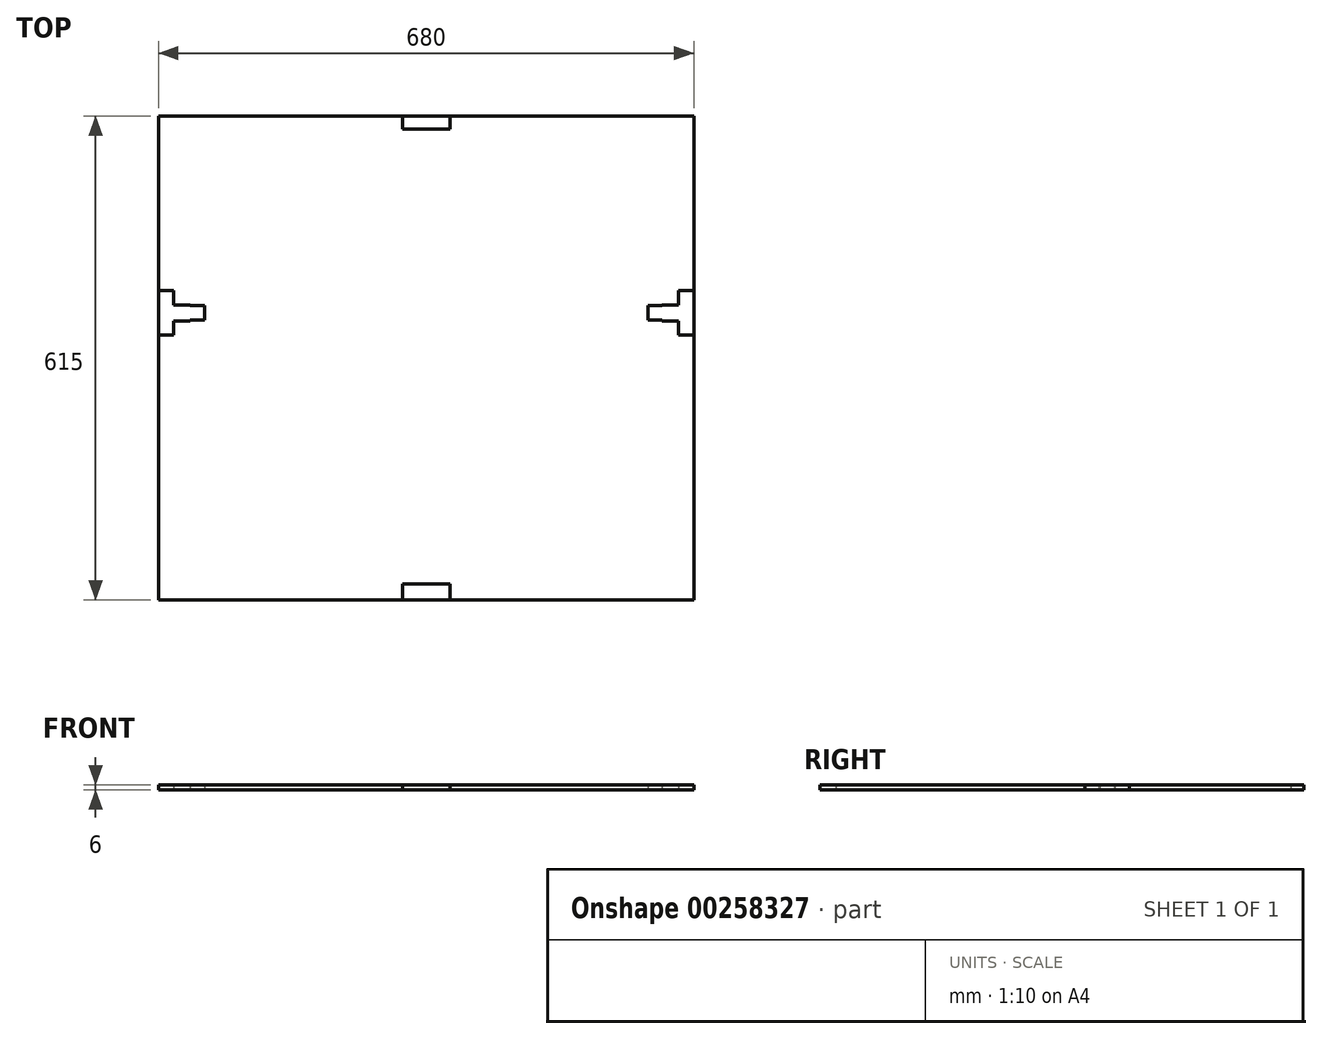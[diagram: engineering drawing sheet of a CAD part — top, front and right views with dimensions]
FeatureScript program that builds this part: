
annotation { "Feature Type Name" : "Feature", "Feature Type Description" : "" }
export const myFeature = defineFeature(function(context is Context, id is Id, definition is map)
    precondition{}
    {
        {
            var Q0;
            Q0=qCreatedBy(makeId("Top.planeOp"),FACE);
            var sketch = newSketch(context, id + "F0", { "sketchPlane" : qUnion([Q0])});
            skLineSegment(sketch, "E0.bottom", {"start": v(340, -307.5) * mm, "end": v(30.2, -307.5) * mm});
            skLineSegment(sketch, "E0.top", {"start": v(340, 307.5) * mm, "end": v(30.2, 307.5) * mm});
            skLineSegment(sketch, "E0.left", {"start": v(340, -307.5) * mm, "end": v(340, 29.3) * mm});
            skLineSegment(sketch, "E0.right", {"start": v(-340, -307.5) * mm, "end": v(-340, 29.3) * mm});
            skPoint(sketch, "E0.middle", {"position": v(0, 0) * mm});
            skLineSegment(sketch, "E1", {"start": v(0, 307.5) * mm, "end": v(0, -307.5) * mm, "construction": true});
            skLineSegment(sketch, "E2", {"start": v(-30.2, 307.5) * mm, "end": v(-30.2, 291.1) * mm});
            skLineSegment(sketch, "E3", {"start": v(-30.2, 291.1) * mm, "end": v(30.2, 291.1) * mm});
            skLineSegment(sketch, "E4", {"start": v(30.2, 291.1) * mm, "end": v(30.2, 307.5) * mm});
            skLineSegment(sketch, "E5.trimOffspring", {"start": v(-30.2, 307.5) * mm, "end": v(-340, 307.5) * mm});
            skLineSegment(sketch, "E6.trimOffspring", {"start": v(-30.2, -307.5) * mm, "end": v(-340, -307.5) * mm});
            skLineSegment(sketch, "E7", {"start": v(-30.2, -307.5) * mm, "end": v(-30.2, -287.1) * mm});
            skLineSegment(sketch, "E8", {"start": v(-30.2, -287.1) * mm, "end": v(30.2, -287.1) * mm});
            skLineSegment(sketch, "E9", {"start": v(30.2, -287.1) * mm, "end": v(30.2, -307.5) * mm});
            skLineSegment(sketch, "E10", {"start": v(-340, 85.7) * mm, "end": v(-320.8, 85.7) * mm});
            skLineSegment(sketch, "E11", {"start": v(-320.8, 85.7) * mm, "end": v(-320.8, 67.7) * mm});
            skLineSegment(sketch, "E12", {"start": v(-299.6, 48.3) * mm, "end": v(-281.6, 48.3) * mm});
            skLineSegment(sketch, "E13", {"start": v(-281.6, 66.7) * mm, "end": v(-281.6, 48.3) * mm});
            skLineSegment(sketch, "E14", {"start": v(-281.6, 66.7) * mm, "end": v(-299.6, 66.7) * mm});
            skLineSegment(sketch, "E15", {"start": v(-320.8, 29.3) * mm, "end": v(-340, 29.3) * mm});
            skLineSegment(sketch, "E16", {"start": v(-299.6, 66.7) * mm, "end": v(-299.6, 67.7) * mm});
            skLineSegment(sketch, "E17", {"start": v(-299.6, 67.7) * mm, "end": v(-320.8, 67.7) * mm});
            skLineSegment(sketch, "E18", {"start": v(-299.6, 48.3) * mm, "end": v(-299.6, 47.3) * mm});
            skLineSegment(sketch, "E19", {"start": v(-299.6, 47.3) * mm, "end": v(-320.8, 47.3) * mm});
            skLineSegment(sketch, "E20.trimOffspring", {"start": v(-320.8, 47.3) * mm, "end": v(-320.8, 29.3) * mm});
            skLineSegment(sketch, "E21.trimOffspring", {"start": v(-340, 85.7) * mm, "end": v(-340, 307.5) * mm});
            skLineSegment(sketch, "E22.MirrorCS", {"start": v(299.6, 48.3) * mm, "end": v(299.6, 47.3) * mm});
            skLineSegment(sketch, "E23.MirrorCS", {"start": v(299.6, 66.7) * mm, "end": v(299.6, 67.7) * mm});
            skLineSegment(sketch, "E24.MirrorCS", {"start": v(299.6, 47.3) * mm, "end": v(320.8, 47.3) * mm});
            skLineSegment(sketch, "E25.MirrorCS", {"start": v(320.8, 29.3) * mm, "end": v(340, 29.3) * mm});
            skLineSegment(sketch, "E26.MirrorCS", {"start": v(299.6, 67.7) * mm, "end": v(320.8, 67.7) * mm});
            skLineSegment(sketch, "E27.MirrorCS", {"start": v(281.6, 66.7) * mm, "end": v(281.6, 48.3) * mm});
            skLineSegment(sketch, "E28.MirrorCS", {"start": v(320.8, 47.3) * mm, "end": v(320.8, 29.3) * mm});
            skLineSegment(sketch, "E29.MirrorCS", {"start": v(340, 85.7) * mm, "end": v(320.8, 85.7) * mm});
            skLineSegment(sketch, "E30.MirrorCS", {"start": v(299.6, 48.3) * mm, "end": v(281.6, 48.3) * mm});
            skLineSegment(sketch, "E31.MirrorCS", {"start": v(281.6, 66.7) * mm, "end": v(299.6, 66.7) * mm});
            skLineSegment(sketch, "E32.MirrorCS", {"start": v(320.8, 85.7) * mm, "end": v(320.8, 67.7) * mm});
            skLineSegment(sketch, "E33.trimOffspring", {"start": v(340, 85.7) * mm, "end": v(340, 307.5) * mm});
            skLineSegment(sketch, "E34", {"start": v(-330, 85.7) * mm, "end": v(-330, 29.3) * mm, "construction": true});
            skLineSegment(sketch, "E35", {"start": v(-281.6, 57.5) * mm, "end": v(-330, 57.5) * mm, "construction": true});
            skSolve(sketch);
        }
        {
            var Q0;
            Q0=qCreatedBy(makeId("Top.planeOp"),FACE);
            var sketch = newSketch(context, id + "F1", { "sketchPlane" : qUnion([Q0])});
            skLineSegment(sketch, "E36.bottom", {"start": v(-340, 307.5) * mm, "end": v(340, 307.5) * mm});
            skLineSegment(sketch, "E36.top", {"start": v(-340, -307.5) * mm, "end": v(340, -307.5) * mm});
            skLineSegment(sketch, "E36.left", {"start": v(-340, 307.5) * mm, "end": v(-340, -307.5) * mm});
            skLineSegment(sketch, "E36.right", {"start": v(340, 307.5) * mm, "end": v(340, -307.5) * mm});
            skSolve(sketch);
        }
        {
            var Q0;
            Q0 = qSketchRegion(id + "F1", true);
            extrude(context, id + "F2", {"entities" : qUnion([Q0]), "depth" : 6 * mm, "offsetDistance" : 25 * mm});
        }
        {
            var Q0;
            Q0=qSketchRegion(id+"F0",true);
            extrude(context, id + "F3", {"entities" : qUnion([Q0]), "depth" : 6 * mm});
        }
    });
